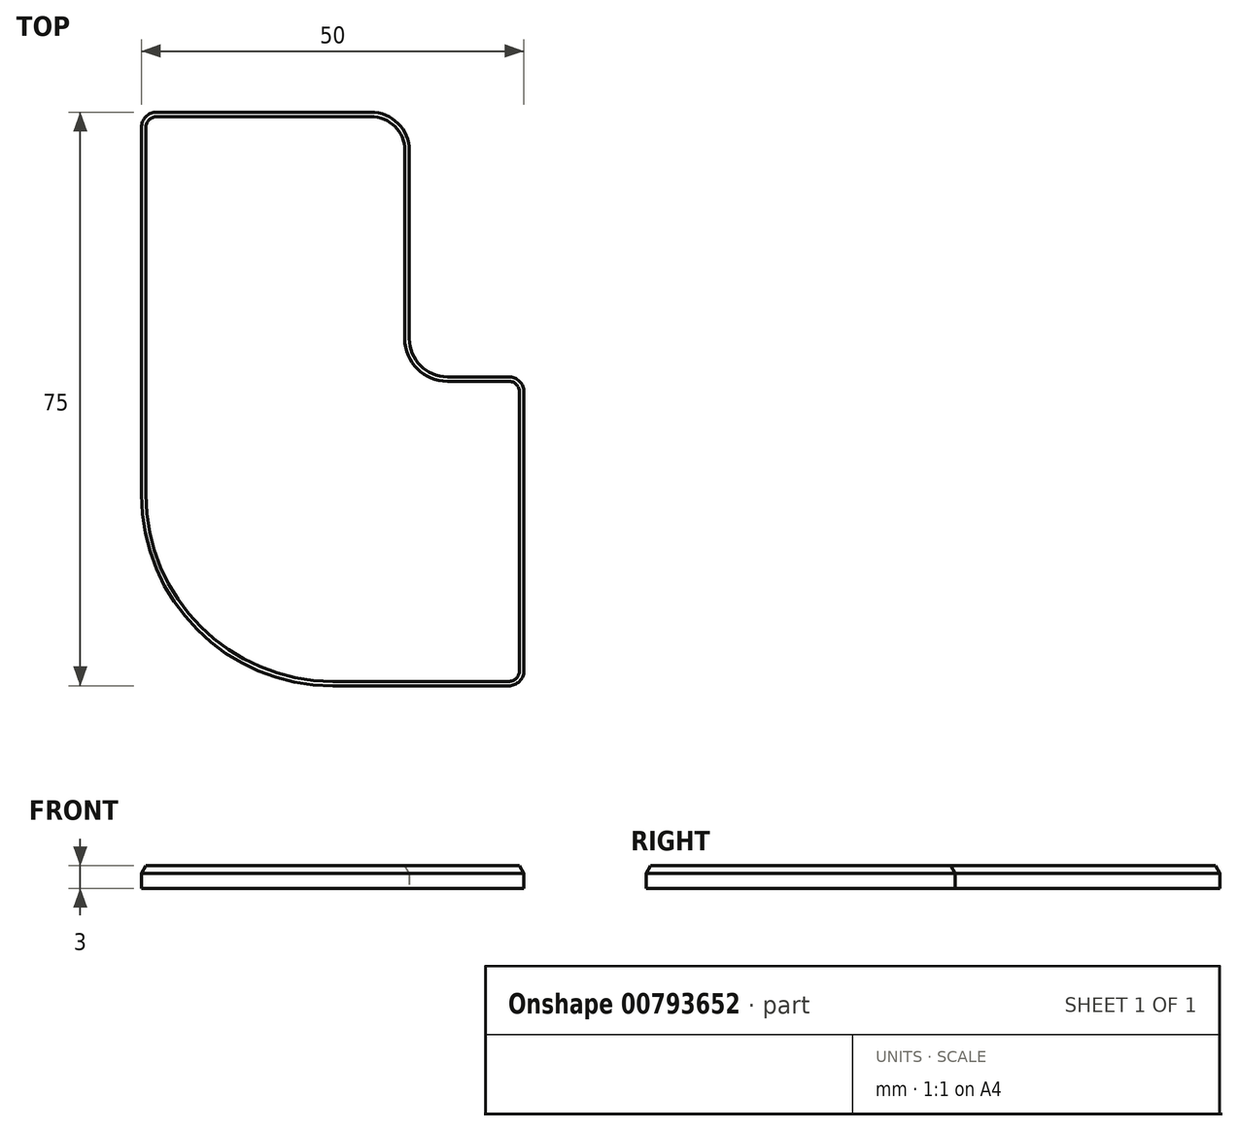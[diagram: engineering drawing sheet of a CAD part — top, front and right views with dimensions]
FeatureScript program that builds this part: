
annotation { "Feature Type Name" : "Feature", "Feature Type Description" : "" }
export const myFeature = defineFeature(function(context is Context, id is Id, definition is map)
    precondition{}
    {
        {
            var Q0;
            Q0=qCreatedBy(makeId("Top.planeOp"),FACE);
            var sketch = newSketch(context, id + "F0", { "sketchPlane" : qUnion([Q0])});
            skLineSegment(sketch, "E0", {"start": v(0, 0) * mm, "end": v(0, 32.6) * mm});
            skLineSegment(sketch, "E1", {"start": v(2, 34.6) * mm, "end": v(30, 34.6) * mm});
            skLineSegment(sketch, "E2", {"start": v(35, 29.6) * mm, "end": v(35, 5) * mm});
            skLineSegment(sketch, "E3", {"start": v(40, 0) * mm, "end": v(48, 0) * mm});
            skLineSegment(sketch, "E4", {"start": v(50, -2) * mm, "end": v(50, -38.4) * mm});
            skLineSegment(sketch, "E5", {"start": v(48, -40.4) * mm, "end": v(25, -40.4) * mm});
            skLineSegment(sketch, "E6", {"start": v(0, -15.4) * mm, "end": v(0, 0) * mm});
            skPoint(sketch, "E7.visualSharp", {"position": v(35, 0) * mm});
            skArc(sketch, "E7.filletArc", {"start": v(35, 5) * mm, "mid": v(36.46, 1.46) * mm, "end": v(40, 0) * mm});
            skPoint(sketch, "E8.visualSharp", {"position": v(35, 34.6) * mm});
            skArc(sketch, "E8.filletArc", {"start": v(35, 29.6) * mm, "mid": v(33.54, 33.14) * mm, "end": v(30, 34.6) * mm});
            skPoint(sketch, "E9.visualSharp", {"position": v(0, -40.4) * mm});
            skArc(sketch, "E9.filletArc", {"start": v(0, -15.4) * mm, "mid": v(7.32, -33.08) * mm, "end": v(25, -40.4) * mm});
            skPoint(sketch, "E10.visualSharp", {"position": v(0, 34.6) * mm});
            skArc(sketch, "E10.filletArc", {"start": v(2, 34.6) * mm, "mid": v(0.59, 34.01) * mm, "end": v(0, 32.6) * mm});
            skPoint(sketch, "E11.visualSharp", {"position": v(50, -40.4) * mm});
            skArc(sketch, "E11.filletArc", {"start": v(48, -40.4) * mm, "mid": v(49.41, -39.81) * mm, "end": v(50, -38.4) * mm});
            skPoint(sketch, "E12.visualSharp", {"position": v(50, 0) * mm});
            skArc(sketch, "E12.filletArc", {"start": v(50, -2) * mm, "mid": v(49.41, -0.59) * mm, "end": v(48, 0) * mm});
            skSolve(sketch);
        }
        {
            var Q0;
            Q0 = qSketchRegion(id + "F0", true);
            extrude(context, id + "F1", {"entities" : qUnion([Q0]), "depth" : 3 * mm, "offsetDistance" : 25 * mm});
        }
        {
            var Q0;
            Q0=makeQuery(id+"F1.opExtrude","CAP_EDGE",EDGE,{"disambiguationData":[OSD([sQuery(id+"F0.wireOp",EDGE,"E0"),sQuery(id+"F0.wireOp",EDGE,"E6")])],"isStart":false});
            chamfer(context, id + "F2", {"entities" : qUnion([Q0]), "chamferType" : ChamferType.OFFSET_ANGLE, "width" : 1 * mm, "oppositeDirection" : false, "angle" : 30 * degree, "tangentPropagation" : true});
        }
    });
